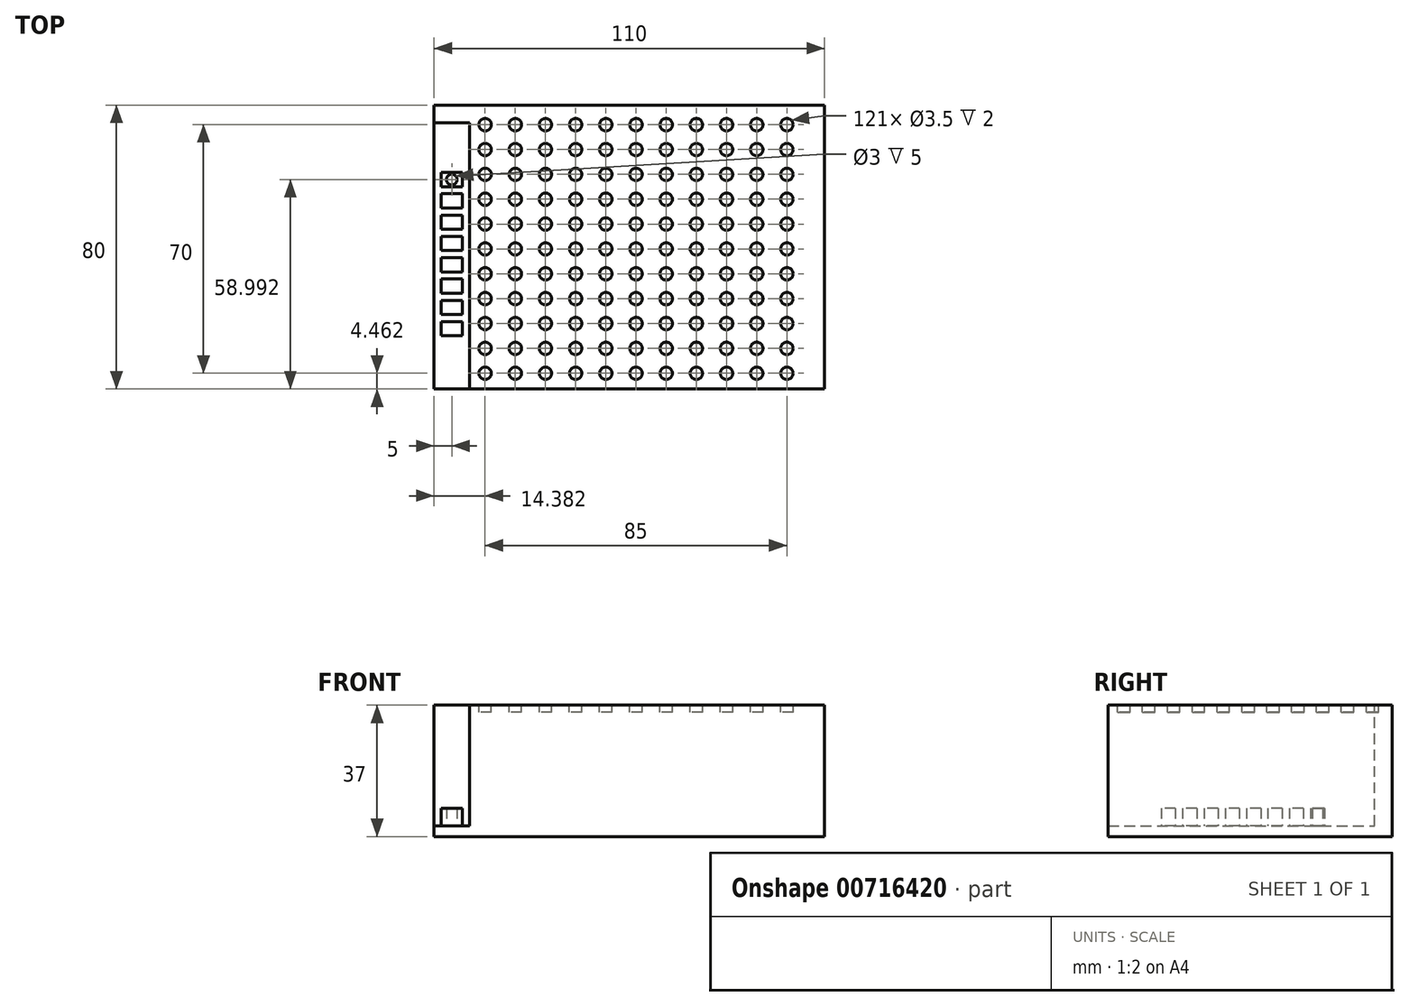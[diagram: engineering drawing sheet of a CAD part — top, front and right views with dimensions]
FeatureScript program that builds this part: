
annotation { "Feature Type Name" : "Feature", "Feature Type Description" : "" }
export const myFeature = defineFeature(function(context is Context, id is Id, definition is map)
    precondition{}
    {
        {
            var Q0;
            Q0=qCreatedBy(makeId("Top.planeOp"),FACE);
            var sketch = newSketch(context, id + "F0", { "sketchPlane" : qUnion([Q0])});
            skLineSegment(sketch, "E0.bottom", {"start": v(0, 0) * mm, "end": v(110, 0) * mm});
            skLineSegment(sketch, "E0.top", {"start": v(0, 80) * mm, "end": v(110, 80) * mm});
            skLineSegment(sketch, "E0.left", {"start": v(0, 0) * mm, "end": v(0, 80) * mm});
            skLineSegment(sketch, "E0.right", {"start": v(110, 0) * mm, "end": v(110, 80) * mm});
            skSolve(sketch);
        }
        {
            var Q0;
            Q0 = qSketchRegion(id + "F0", true);
            extrude(context, id + "F1", {"entities" : qUnion([Q0]), "flatOperationType" : FlatOperationType.REMOVE, "depth" : 37 * mm, "offsetDistance" : 25 * mm, "domain" : OperationDomain.MODEL});
        }
        {
            var Q0;
            Q0=makeQuery(id+"F1.opExtrude","CAP_FACE",FACE,{"disambiguationData":[OSD([sQuery(id+"F0.wireOp",EDGE,"E0.bottom"),sQuery(id+"F0.wireOp",EDGE,"E0.top"),sQuery(id+"F0.wireOp",EDGE,"E0.left"),sQuery(id+"F0.wireOp",EDGE,"E0.right")])],"isStart":false});
            var sketch = newSketch(context, id + "F2", { "sketchPlane" : qUnion([Q0])});
            skLineSegment(sketch, "E1.bottom", {"start": v(10, 0) * mm, "end": v(0, 0) * mm});
            skLineSegment(sketch, "E1.top", {"start": v(10, 75) * mm, "end": v(0, 75) * mm});
            skLineSegment(sketch, "E1.left", {"start": v(10, 0) * mm, "end": v(10, 75) * mm});
            skLineSegment(sketch, "E1.right", {"start": v(0, 0) * mm, "end": v(0, 75) * mm});
            skSolve(sketch);
        }
        {
            var Q0;
            Q0 = qSketchRegion(id + "F2", true);
            extrude(context, id + "F3", {"entities" : qUnion([Q0]), "operationType" : NewBodyOperationType.REMOVE, "flatOperationType" : FlatOperationType.REMOVE, "oppositeDirection" : true, "depth" : 34 * mm, "offsetDistance" : 25 * mm, "domain" : OperationDomain.MODEL});
        }
        {
            var Q0;
            Q0=makeQuery(id+"F1.opExtrude","CAP_FACE",FACE,{"disambiguationData":[OSD([sQuery(id+"F0.wireOp",EDGE,"E0.bottom"),sQuery(id+"F0.wireOp",EDGE,"E0.top"),sQuery(id+"F0.wireOp",EDGE,"E0.left"),sQuery(id+"F0.wireOp",EDGE,"E0.right")])],"isStart":false});
            var sketch = newSketch(context, id + "F4", { "sketchPlane" : qUnion([Q0])});
            skCircle(sketch, "E2", {"center": v(14.38, 4.46) * mm, "radius": 1.75 * mm});
            skCircle(sketch, "E3.0.1.0", {"center": v(14.38, 11.46) * mm, "radius": 1.75 * mm});
            skCircle(sketch, "E3.0.2.0", {"center": v(14.38, 18.46) * mm, "radius": 1.75 * mm});
            skCircle(sketch, "E3.0.3.0", {"center": v(14.38, 25.46) * mm, "radius": 1.75 * mm});
            skCircle(sketch, "E3.0.4.0", {"center": v(14.38, 32.46) * mm, "radius": 1.75 * mm});
            skCircle(sketch, "E3.0.5.0", {"center": v(14.38, 39.46) * mm, "radius": 1.75 * mm});
            skCircle(sketch, "E3.0.6.0", {"center": v(14.38, 46.46) * mm, "radius": 1.75 * mm});
            skCircle(sketch, "E3.0.7.0", {"center": v(14.38, 53.46) * mm, "radius": 1.75 * mm});
            skCircle(sketch, "E3.1.0.0", {"center": v(22.88, 4.46) * mm, "radius": 1.75 * mm});
            skCircle(sketch, "E3.1.1.0", {"center": v(22.88, 11.46) * mm, "radius": 1.75 * mm});
            skCircle(sketch, "E3.1.2.0", {"center": v(22.88, 18.46) * mm, "radius": 1.75 * mm});
            skCircle(sketch, "E3.1.3.0", {"center": v(22.88, 25.46) * mm, "radius": 1.75 * mm});
            skCircle(sketch, "E3.1.4.0", {"center": v(22.88, 32.46) * mm, "radius": 1.75 * mm});
            skCircle(sketch, "E3.1.5.0", {"center": v(22.88, 39.46) * mm, "radius": 1.75 * mm});
            skCircle(sketch, "E3.1.6.0", {"center": v(22.88, 46.46) * mm, "radius": 1.75 * mm});
            skCircle(sketch, "E3.1.7.0", {"center": v(22.88, 53.46) * mm, "radius": 1.75 * mm});
            skCircle(sketch, "E3.2.0.0", {"center": v(31.38, 4.46) * mm, "radius": 1.75 * mm});
            skCircle(sketch, "E3.2.1.0", {"center": v(31.38, 11.46) * mm, "radius": 1.75 * mm});
            skCircle(sketch, "E3.2.2.0", {"center": v(31.38, 18.46) * mm, "radius": 1.75 * mm});
            skCircle(sketch, "E3.2.3.0", {"center": v(31.38, 25.46) * mm, "radius": 1.75 * mm});
            skCircle(sketch, "E3.2.4.0", {"center": v(31.38, 32.46) * mm, "radius": 1.75 * mm});
            skCircle(sketch, "E3.2.5.0", {"center": v(31.38, 39.46) * mm, "radius": 1.75 * mm});
            skCircle(sketch, "E3.2.6.0", {"center": v(31.38, 46.46) * mm, "radius": 1.75 * mm});
            skCircle(sketch, "E3.2.7.0", {"center": v(31.38, 53.46) * mm, "radius": 1.75 * mm});
            skCircle(sketch, "E3.3.0.0", {"center": v(39.88, 4.46) * mm, "radius": 1.75 * mm});
            skCircle(sketch, "E3.3.1.0", {"center": v(39.88, 11.46) * mm, "radius": 1.75 * mm});
            skCircle(sketch, "E3.3.2.0", {"center": v(39.88, 18.46) * mm, "radius": 1.75 * mm});
            skCircle(sketch, "E3.3.3.0", {"center": v(39.88, 25.46) * mm, "radius": 1.75 * mm});
            skCircle(sketch, "E3.3.4.0", {"center": v(39.88, 32.46) * mm, "radius": 1.75 * mm});
            skCircle(sketch, "E3.3.5.0", {"center": v(39.88, 39.46) * mm, "radius": 1.75 * mm});
            skCircle(sketch, "E3.3.6.0", {"center": v(39.88, 46.46) * mm, "radius": 1.75 * mm});
            skCircle(sketch, "E3.3.7.0", {"center": v(39.88, 53.46) * mm, "radius": 1.75 * mm});
            skCircle(sketch, "E3.4.0.0", {"center": v(48.38, 4.46) * mm, "radius": 1.75 * mm});
            skCircle(sketch, "E3.4.1.0", {"center": v(48.38, 11.46) * mm, "radius": 1.75 * mm});
            skCircle(sketch, "E3.4.2.0", {"center": v(48.38, 18.46) * mm, "radius": 1.75 * mm});
            skCircle(sketch, "E3.4.3.0", {"center": v(48.38, 25.46) * mm, "radius": 1.75 * mm});
            skCircle(sketch, "E3.4.4.0", {"center": v(48.38, 32.46) * mm, "radius": 1.75 * mm});
            skCircle(sketch, "E3.4.5.0", {"center": v(48.38, 39.46) * mm, "radius": 1.75 * mm});
            skCircle(sketch, "E3.4.6.0", {"center": v(48.38, 46.46) * mm, "radius": 1.75 * mm});
            skCircle(sketch, "E3.4.7.0", {"center": v(48.38, 53.46) * mm, "radius": 1.75 * mm});
            skCircle(sketch, "E3.5.0.0", {"center": v(56.88, 4.46) * mm, "radius": 1.75 * mm});
            skCircle(sketch, "E3.5.1.0", {"center": v(56.88, 11.46) * mm, "radius": 1.75 * mm});
            skCircle(sketch, "E3.5.2.0", {"center": v(56.88, 18.46) * mm, "radius": 1.75 * mm});
            skCircle(sketch, "E3.5.3.0", {"center": v(56.88, 25.46) * mm, "radius": 1.75 * mm});
            skCircle(sketch, "E3.5.4.0", {"center": v(56.88, 32.46) * mm, "radius": 1.75 * mm});
            skCircle(sketch, "E3.5.5.0", {"center": v(56.88, 39.46) * mm, "radius": 1.75 * mm});
            skCircle(sketch, "E3.5.6.0", {"center": v(56.88, 46.46) * mm, "radius": 1.75 * mm});
            skCircle(sketch, "E3.5.7.0", {"center": v(56.88, 53.46) * mm, "radius": 1.75 * mm});
            skCircle(sketch, "E3.6.0.0", {"center": v(65.38, 4.46) * mm, "radius": 1.75 * mm});
            skCircle(sketch, "E3.6.1.0", {"center": v(65.38, 11.46) * mm, "radius": 1.75 * mm});
            skCircle(sketch, "E3.6.2.0", {"center": v(65.38, 18.46) * mm, "radius": 1.75 * mm});
            skCircle(sketch, "E3.6.3.0", {"center": v(65.38, 25.46) * mm, "radius": 1.75 * mm});
            skCircle(sketch, "E3.6.4.0", {"center": v(65.38, 32.46) * mm, "radius": 1.75 * mm});
            skCircle(sketch, "E3.6.5.0", {"center": v(65.38, 39.46) * mm, "radius": 1.75 * mm});
            skCircle(sketch, "E3.6.6.0", {"center": v(65.38, 46.46) * mm, "radius": 1.75 * mm});
            skCircle(sketch, "E3.6.7.0", {"center": v(65.38, 53.46) * mm, "radius": 1.75 * mm});
            skCircle(sketch, "E3.7.0.0", {"center": v(73.88, 4.46) * mm, "radius": 1.75 * mm});
            skCircle(sketch, "E3.7.1.0", {"center": v(73.88, 11.46) * mm, "radius": 1.75 * mm});
            skCircle(sketch, "E3.7.2.0", {"center": v(73.88, 18.46) * mm, "radius": 1.75 * mm});
            skCircle(sketch, "E3.7.3.0", {"center": v(73.88, 25.46) * mm, "radius": 1.75 * mm});
            skCircle(sketch, "E3.7.4.0", {"center": v(73.88, 32.46) * mm, "radius": 1.75 * mm});
            skCircle(sketch, "E3.7.5.0", {"center": v(73.88, 39.46) * mm, "radius": 1.75 * mm});
            skCircle(sketch, "E3.7.6.0", {"center": v(73.88, 46.46) * mm, "radius": 1.75 * mm});
            skCircle(sketch, "E3.7.7.0", {"center": v(73.88, 53.46) * mm, "radius": 1.75 * mm});
            skCircle(sketch, "E3.8.0.0", {"center": v(82.38, 4.46) * mm, "radius": 1.75 * mm});
            skCircle(sketch, "E3.8.1.0", {"center": v(82.38, 11.46) * mm, "radius": 1.75 * mm});
            skCircle(sketch, "E3.8.2.0", {"center": v(82.38, 18.46) * mm, "radius": 1.75 * mm});
            skCircle(sketch, "E3.8.3.0", {"center": v(82.38, 25.46) * mm, "radius": 1.75 * mm});
            skCircle(sketch, "E3.8.4.0", {"center": v(82.38, 32.46) * mm, "radius": 1.75 * mm});
            skCircle(sketch, "E3.8.5.0", {"center": v(82.38, 39.46) * mm, "radius": 1.75 * mm});
            skCircle(sketch, "E3.8.6.0", {"center": v(82.38, 46.46) * mm, "radius": 1.75 * mm});
            skCircle(sketch, "E3.8.7.0", {"center": v(82.38, 53.46) * mm, "radius": 1.75 * mm});
            skLineSegment(sketch, "E3.direction1", {"start": v(14.38, 4.46) * mm, "end": v(22.88, 4.46) * mm, "construction": true});
            skLineSegment(sketch, "E3.direction2", {"start": v(14.38, 4.46) * mm, "end": v(14.38, 11.46) * mm, "construction": true});
            skCircle(sketch, "E4.0.0.8", {"center": v(14.38, 60.46) * mm, "radius": 1.75 * mm});
            skCircle(sketch, "E4.0.0.9", {"center": v(14.38, 67.46) * mm, "radius": 1.75 * mm});
            skCircle(sketch, "E4.0.0.10", {"center": v(14.38, 74.46) * mm, "radius": 1.75 * mm});
            skCircle(sketch, "E4.0.1.8", {"center": v(22.88, 60.46) * mm, "radius": 1.75 * mm});
            skCircle(sketch, "E4.0.1.9", {"center": v(22.88, 67.46) * mm, "radius": 1.75 * mm});
            skCircle(sketch, "E4.0.1.10", {"center": v(22.88, 74.46) * mm, "radius": 1.75 * mm});
            skCircle(sketch, "E4.0.2.8", {"center": v(31.38, 60.46) * mm, "radius": 1.75 * mm});
            skCircle(sketch, "E4.0.2.9", {"center": v(31.38, 67.46) * mm, "radius": 1.75 * mm});
            skCircle(sketch, "E4.0.2.10", {"center": v(31.38, 74.46) * mm, "radius": 1.75 * mm});
            skCircle(sketch, "E4.0.3.8", {"center": v(39.88, 60.46) * mm, "radius": 1.75 * mm});
            skCircle(sketch, "E4.0.3.9", {"center": v(39.88, 67.46) * mm, "radius": 1.75 * mm});
            skCircle(sketch, "E4.0.3.10", {"center": v(39.88, 74.46) * mm, "radius": 1.75 * mm});
            skCircle(sketch, "E4.0.4.8", {"center": v(48.38, 60.46) * mm, "radius": 1.75 * mm});
            skCircle(sketch, "E4.0.4.9", {"center": v(48.38, 67.46) * mm, "radius": 1.75 * mm});
            skCircle(sketch, "E4.0.4.10", {"center": v(48.38, 74.46) * mm, "radius": 1.75 * mm});
            skCircle(sketch, "E4.0.5.8", {"center": v(56.88, 60.46) * mm, "radius": 1.75 * mm});
            skCircle(sketch, "E4.0.5.9", {"center": v(56.88, 67.46) * mm, "radius": 1.75 * mm});
            skCircle(sketch, "E4.0.5.10", {"center": v(56.88, 74.46) * mm, "radius": 1.75 * mm});
            skCircle(sketch, "E4.0.6.8", {"center": v(65.38, 60.46) * mm, "radius": 1.75 * mm});
            skCircle(sketch, "E4.0.6.9", {"center": v(65.38, 67.46) * mm, "radius": 1.75 * mm});
            skCircle(sketch, "E4.0.6.10", {"center": v(65.38, 74.46) * mm, "radius": 1.75 * mm});
            skCircle(sketch, "E4.0.7.8", {"center": v(73.88, 60.46) * mm, "radius": 1.75 * mm});
            skCircle(sketch, "E4.0.7.9", {"center": v(73.88, 67.46) * mm, "radius": 1.75 * mm});
            skCircle(sketch, "E4.0.7.10", {"center": v(73.88, 74.46) * mm, "radius": 1.75 * mm});
            skCircle(sketch, "E4.0.8.8", {"center": v(82.38, 60.46) * mm, "radius": 1.75 * mm});
            skCircle(sketch, "E4.0.8.9", {"center": v(82.38, 67.46) * mm, "radius": 1.75 * mm});
            skCircle(sketch, "E4.0.8.10", {"center": v(82.38, 74.46) * mm, "radius": 1.75 * mm});
            skCircle(sketch, "E5.0.9.0", {"center": v(90.88, 4.46) * mm, "radius": 1.75 * mm});
            skCircle(sketch, "E5.0.9.1", {"center": v(90.88, 11.46) * mm, "radius": 1.75 * mm});
            skCircle(sketch, "E5.0.9.2", {"center": v(90.88, 18.46) * mm, "radius": 1.75 * mm});
            skCircle(sketch, "E5.0.9.3", {"center": v(90.88, 25.46) * mm, "radius": 1.75 * mm});
            skCircle(sketch, "E5.0.9.4", {"center": v(90.88, 32.46) * mm, "radius": 1.75 * mm});
            skCircle(sketch, "E5.0.9.5", {"center": v(90.88, 39.46) * mm, "radius": 1.75 * mm});
            skCircle(sketch, "E5.0.9.6", {"center": v(90.88, 46.46) * mm, "radius": 1.75 * mm});
            skCircle(sketch, "E5.0.9.7", {"center": v(90.88, 53.46) * mm, "radius": 1.75 * mm});
            skCircle(sketch, "E5.0.9.8", {"center": v(90.88, 60.46) * mm, "radius": 1.75 * mm});
            skCircle(sketch, "E5.0.9.9", {"center": v(90.88, 67.46) * mm, "radius": 1.75 * mm});
            skCircle(sketch, "E5.0.9.10", {"center": v(90.88, 74.46) * mm, "radius": 1.75 * mm});
            skCircle(sketch, "E5.0.10.0", {"center": v(99.38, 4.46) * mm, "radius": 1.75 * mm});
            skCircle(sketch, "E5.0.10.1", {"center": v(99.38, 11.46) * mm, "radius": 1.75 * mm});
            skCircle(sketch, "E5.0.10.2", {"center": v(99.38, 18.46) * mm, "radius": 1.75 * mm});
            skCircle(sketch, "E5.0.10.3", {"center": v(99.38, 25.46) * mm, "radius": 1.75 * mm});
            skCircle(sketch, "E5.0.10.4", {"center": v(99.38, 32.46) * mm, "radius": 1.75 * mm});
            skCircle(sketch, "E5.0.10.5", {"center": v(99.38, 39.46) * mm, "radius": 1.75 * mm});
            skCircle(sketch, "E5.0.10.6", {"center": v(99.38, 46.46) * mm, "radius": 1.75 * mm});
            skCircle(sketch, "E5.0.10.7", {"center": v(99.38, 53.46) * mm, "radius": 1.75 * mm});
            skCircle(sketch, "E5.0.10.8", {"center": v(99.38, 60.46) * mm, "radius": 1.75 * mm});
            skCircle(sketch, "E5.0.10.9", {"center": v(99.38, 67.46) * mm, "radius": 1.75 * mm});
            skCircle(sketch, "E5.0.10.10", {"center": v(99.38, 74.46) * mm, "radius": 1.75 * mm});
            skSolve(sketch);
        }
        {
            var Q0;
            Q0 = qSketchRegion(id + "F4", true);
            extrude(context, id + "F5", {"entities" : qUnion([Q0]), "operationType" : NewBodyOperationType.REMOVE, "oppositeDirection" : true, "depth" : 2 * mm, "offsetDistance" : 25 * mm});
        }
        {
            var Q0;
            Q0=makeQuery(id+"F3.boolean.opBoolean","COPY",FACE,{"derivedFrom":makeQuery(id+"F3.opExtrude","CAP_FACE",FACE,{"disambiguationData":[OSD([sQuery(id+"F2.wireOp",EDGE,"E1.bottom"),sQuery(id+"F2.wireOp",EDGE,"E1.top"),sQuery(id+"F2.wireOp",EDGE,"E1.left"),sQuery(id+"F2.wireOp",EDGE,"E1.right")])],"isStart":false})});
            var sketch = newSketch(context, id + "F6", { "sketchPlane" : qUnion([Q0])});
            skLineSegment(sketch, "E6.bottom", {"start": v(8, 60.99) * mm, "end": v(2, 60.99) * mm});
            skLineSegment(sketch, "E6.top", {"start": v(8, 57) * mm, "end": v(2, 57) * mm});
            skLineSegment(sketch, "E6.left", {"start": v(8, 60.99) * mm, "end": v(8, 57) * mm});
            skLineSegment(sketch, "E6.right", {"start": v(2, 60.99) * mm, "end": v(2, 57) * mm});
            skLineSegment(sketch, "E7.0.1.0", {"start": v(2, 54.99) * mm, "end": v(2, 51) * mm});
            skLineSegment(sketch, "E7.0.1.1", {"start": v(8, 54.99) * mm, "end": v(8, 51) * mm});
            skLineSegment(sketch, "E7.0.1.2", {"start": v(8, 51) * mm, "end": v(2, 51) * mm});
            skLineSegment(sketch, "E7.0.1.3", {"start": v(8, 54.99) * mm, "end": v(2, 54.99) * mm});
            skLineSegment(sketch, "E7.0.2.0", {"start": v(2, 48.99) * mm, "end": v(2, 45) * mm});
            skLineSegment(sketch, "E7.0.2.1", {"start": v(8, 48.99) * mm, "end": v(8, 45) * mm});
            skLineSegment(sketch, "E7.0.2.2", {"start": v(8, 45) * mm, "end": v(2, 45) * mm});
            skLineSegment(sketch, "E7.0.2.3", {"start": v(8, 48.99) * mm, "end": v(2, 48.99) * mm});
            skLineSegment(sketch, "E7.0.3.0", {"start": v(2, 42.99) * mm, "end": v(2, 39) * mm});
            skLineSegment(sketch, "E7.0.3.1", {"start": v(8, 42.99) * mm, "end": v(8, 39) * mm});
            skLineSegment(sketch, "E7.0.3.2", {"start": v(8, 39) * mm, "end": v(2, 39) * mm});
            skLineSegment(sketch, "E7.0.3.3", {"start": v(8, 42.99) * mm, "end": v(2, 42.99) * mm});
            skLineSegment(sketch, "E7.0.4.0", {"start": v(2, 36.99) * mm, "end": v(2, 33) * mm});
            skLineSegment(sketch, "E7.0.4.1", {"start": v(8, 36.99) * mm, "end": v(8, 33) * mm});
            skLineSegment(sketch, "E7.0.4.2", {"start": v(8, 33) * mm, "end": v(2, 33) * mm});
            skLineSegment(sketch, "E7.0.4.3", {"start": v(8, 36.99) * mm, "end": v(2, 36.99) * mm});
            skLineSegment(sketch, "E7.0.5.0", {"start": v(2, 30.99) * mm, "end": v(2, 27) * mm});
            skLineSegment(sketch, "E7.0.5.1", {"start": v(8, 30.99) * mm, "end": v(8, 27) * mm});
            skLineSegment(sketch, "E7.0.5.2", {"start": v(8, 27) * mm, "end": v(2, 27) * mm});
            skLineSegment(sketch, "E7.0.5.3", {"start": v(8, 30.99) * mm, "end": v(2, 30.99) * mm});
            skLineSegment(sketch, "E7.0.6.0", {"start": v(2, 24.99) * mm, "end": v(2, 21) * mm});
            skLineSegment(sketch, "E7.0.6.1", {"start": v(8, 24.99) * mm, "end": v(8, 21) * mm});
            skLineSegment(sketch, "E7.0.6.2", {"start": v(8, 21) * mm, "end": v(2, 21) * mm});
            skLineSegment(sketch, "E7.0.6.3", {"start": v(8, 24.99) * mm, "end": v(2, 24.99) * mm});
            skLineSegment(sketch, "E7.0.7.0", {"start": v(2, 18.99) * mm, "end": v(2, 15) * mm});
            skLineSegment(sketch, "E7.0.7.1", {"start": v(8, 18.99) * mm, "end": v(8, 15) * mm});
            skLineSegment(sketch, "E7.0.7.2", {"start": v(8, 15) * mm, "end": v(2, 15) * mm});
            skLineSegment(sketch, "E7.0.7.3", {"start": v(8, 18.99) * mm, "end": v(2, 18.99) * mm});
            skLineSegment(sketch, "E7.direction1", {"start": v(2, 57) * mm, "end": v(26.62, 57) * mm, "construction": true});
            skLineSegment(sketch, "E7.direction2", {"start": v(2, 57) * mm, "end": v(2, 51) * mm, "construction": true});
            skCircle(sketch, "E8", {"center": v(5, 59) * mm, "radius": 1.5 * mm});
            skPoint(sketch, "E8.centerSnap0", {"position": v(2, 59) * mm});
            skPoint(sketch, "E8.centerSnap1", {"position": v(5, 60.99) * mm});
            skSolve(sketch);
        }
        {
            var Q0;
            Q0 = qSketchRegion(id + "F6", true);
            extrude(context, id + "F7", {"entities" : qUnion([Q0]), "operationType" : NewBodyOperationType.ADD, "depth" : 5 * mm, "offsetDistance" : 25 * mm});
        }
    });
